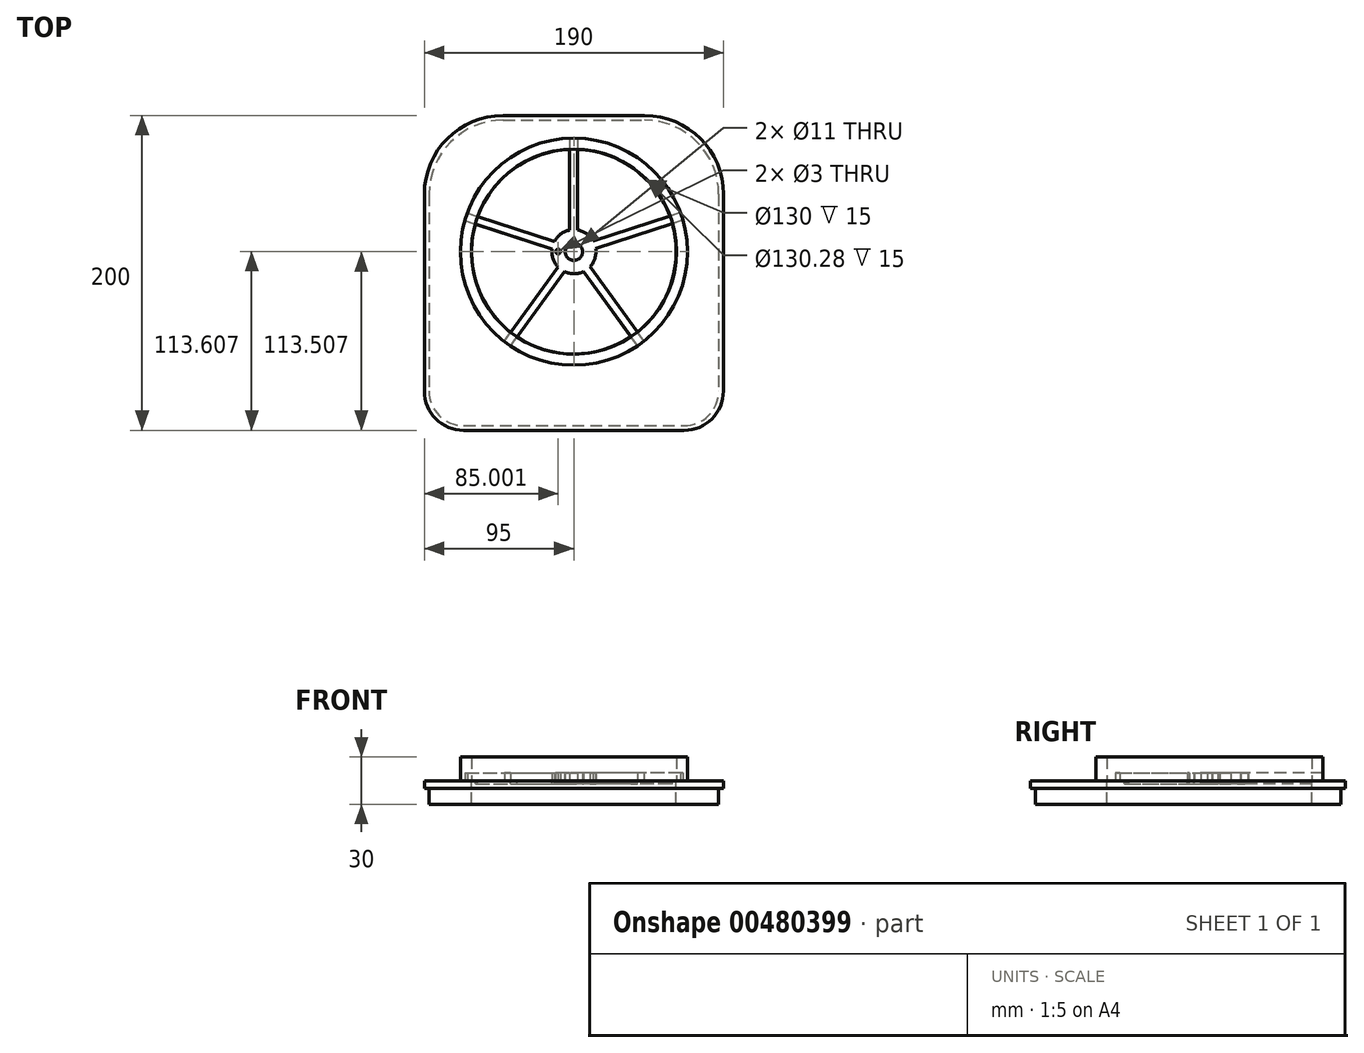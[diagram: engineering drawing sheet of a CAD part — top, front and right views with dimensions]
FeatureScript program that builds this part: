
annotation { "Feature Type Name" : "Feature", "Feature Type Description" : "" }
export const myFeature = defineFeature(function(context is Context, id is Id, definition is map)
    precondition{}
    {
        {
            var Q0;
            Q0=qCreatedBy(makeId("Top.planeOp"),FACE);
            var sketch = newSketch(context, id + "F0", { "sketchPlane" : qUnion([Q0])});
            skLineSegment(sketch, "E0.bottom", {"start": v(49, 200) * mm, "end": v(139, 200) * mm});
            skLineSegment(sketch, "E0.top", {"start": v(24, 0) * mm, "end": v(164, 0) * mm});
            skLineSegment(sketch, "E0.left", {"start": v(-1, 150) * mm, "end": v(-1, 25) * mm});
            skLineSegment(sketch, "E0.right", {"start": v(189, 150) * mm, "end": v(189, 25) * mm});
            skPoint(sketch, "E1.visualSharp", {"position": v(-1, 200) * mm});
            skArc(sketch, "E1.filletArc", {"start": v(49, 200) * mm, "mid": v(13.64, 185.36) * mm, "end": v(-1, 150) * mm});
            skPoint(sketch, "E2.visualSharp", {"position": v(189, 200) * mm});
            skArc(sketch, "E2.filletArc", {"start": v(189, 150) * mm, "mid": v(174.36, 185.36) * mm, "end": v(139, 200) * mm});
            skPoint(sketch, "E3.visualSharp", {"position": v(-1, 0) * mm});
            skArc(sketch, "E3.filletArc", {"start": v(-1, 25) * mm, "mid": v(6.32, 7.32) * mm, "end": v(24, 0) * mm});
            skPoint(sketch, "E4.visualSharp", {"position": v(189, 0) * mm});
            skArc(sketch, "E4.filletArc", {"start": v(164, 0) * mm, "mid": v(181.68, 7.32) * mm, "end": v(189, 25) * mm});
            skSolve(sketch);
        }
        {
            var Q0;
            Q0=makeQuery(id+"F0.imprint","IMPRINT",FACE,{"disambiguationData":[TD([[makeQuery(id+"F0.imprint","IMPRINT",EDGE,{"derivedFrom":sQuery(id+"F0.wireOp",EDGE,"E0.bottom")}),-1.0]])]});
            extrude(context, id + "F1", {"entities" : qUnion([Q0]), "depth" : 5 * mm});
        }
        {
            var Q0;
            Q0=makeQuery(id+"F1.opExtrude","CAP_FACE",FACE,{"disambiguationData":[OSD([sQuery(id+"F0.wireOp",EDGE,"E0.bottom"),sQuery(id+"F0.wireOp",EDGE,"E0.top"),sQuery(id+"F0.wireOp",EDGE,"E0.left"),sQuery(id+"F0.wireOp",EDGE,"E0.right"),sQuery(id+"F0.wireOp",EDGE,"E1.filletArc"),sQuery(id+"F0.wireOp",EDGE,"E2.filletArc"),sQuery(id+"F0.wireOp",EDGE,"E3.filletArc"),sQuery(id+"F0.wireOp",EDGE,"E4.filletArc")])],"isStart":true});
            var sketch = newSketch(context, id + "F2", { "sketchPlane" : qUnion([Q0])});
            skArc(sketch, "E5.0", {"start": v(186, -150) * mm, "mid": v(172.23, -183.23) * mm, "end": v(139, -197) * mm});
            skLineSegment(sketch, "E5.1", {"start": v(49, -197) * mm, "end": v(139, -197) * mm});
            skLineSegment(sketch, "E5.2", {"start": v(186, -150) * mm, "end": v(186, -25) * mm});
            skArc(sketch, "E5.3", {"start": v(49, -197) * mm, "mid": v(15.77, -183.23) * mm, "end": v(2, -150) * mm});
            skArc(sketch, "E5.4", {"start": v(164, -3) * mm, "mid": v(179.56, -9.44) * mm, "end": v(186, -25) * mm});
            skLineSegment(sketch, "E5.5", {"start": v(24, -3) * mm, "end": v(164, -3) * mm});
            skArc(sketch, "E5.6", {"start": v(2, -25) * mm, "mid": v(8.44, -9.44) * mm, "end": v(24, -3) * mm});
            skLineSegment(sketch, "E5.7", {"start": v(2, -150) * mm, "end": v(2, -25) * mm});
            skSolve(sketch);
        }
        {
            var Q0;
            Q0=makeQuery(id+"F2.imprint","IMPRINT",FACE,{"disambiguationData":[TD([[makeQuery(id+"F2.imprint","IMPRINT",EDGE,{"derivedFrom":sQuery(id+"F2.wireOp",EDGE,"E5.0")}),1.0]])]});
            extrude(context, id + "F3", {"entities" : qUnion([Q0]), "operationType" : NewBodyOperationType.ADD, "depth" : 10 * mm});
        }
        {
            var Q0;
            Q0=makeQuery(id+"F1.opExtrude","CAP_FACE",FACE,{"disambiguationData":[OSD([sQuery(id+"F0.wireOp",EDGE,"E0.bottom"),sQuery(id+"F0.wireOp",EDGE,"E0.top"),sQuery(id+"F0.wireOp",EDGE,"E0.left"),sQuery(id+"F0.wireOp",EDGE,"E0.right"),sQuery(id+"F0.wireOp",EDGE,"E1.filletArc"),sQuery(id+"F0.wireOp",EDGE,"E2.filletArc"),sQuery(id+"F0.wireOp",EDGE,"E3.filletArc"),sQuery(id+"F0.wireOp",EDGE,"E4.filletArc")])],"isStart":false});
            var sketch = newSketch(context, id + "F4", { "sketchPlane" : qUnion([Q0])});
            skCircle(sketch, "E6", {"center": v(94, 113.5) * mm, "radius": 65 * mm});
            skSolve(sketch);
        }
        {
            var Q0;
            Q0=makeQuery(id+"F4.imprint","IMPRINT",FACE,{"disambiguationData":[TD([[makeQuery(id+"F4.imprint","IMPRINT",EDGE,{"derivedFrom":sQuery(id+"F4.wireOp",EDGE,"E6")}),1.0]])]});
            extrude(context, id + "F5", {"entities" : qUnion([Q0]), "operationType" : NewBodyOperationType.REMOVE, "oppositeDirection" : true, "depth" : 25 * mm});
        }
        {
            var Q0;
            Q0=makeQuery(id+"F1.opExtrude","CAP_FACE",FACE,{"disambiguationData":[OSD([sQuery(id+"F0.wireOp",EDGE,"E0.bottom"),sQuery(id+"F0.wireOp",EDGE,"E0.top"),sQuery(id+"F0.wireOp",EDGE,"E0.left"),sQuery(id+"F0.wireOp",EDGE,"E0.right"),sQuery(id+"F0.wireOp",EDGE,"E1.filletArc"),sQuery(id+"F0.wireOp",EDGE,"E2.filletArc"),sQuery(id+"F0.wireOp",EDGE,"E3.filletArc"),sQuery(id+"F0.wireOp",EDGE,"E4.filletArc")])],"isStart":false});
            var sketch = newSketch(context, id + "F6", { "sketchPlane" : qUnion([Q0])});
            skArc(sketch, "E7", {"start": v(91.35, 127.25) * mm, "mid": v(85.65, 124.74) * mm, "end": v(81.6, 120) * mm});
            skLineSegment(sketch, "E8.left", {"start": v(91.35, 185.45) * mm, "end": v(91.35, 127.25) * mm});
            skLineSegment(sketch, "E8.right", {"start": v(96.35, 185.45) * mm, "end": v(96.35, 127.3) * mm});
            skLineSegment(sketch, "E9", {"start": v(91.35, 185.45) * mm, "end": v(96.35, 185.45) * mm});
            skLineSegment(sketch, "E10.1.0", {"start": v(24.76, 133.22) * mm, "end": v(80.1, 115.23) * mm});
            skLineSegment(sketch, "E10.1.1", {"start": v(26.3, 137.97) * mm, "end": v(81.6, 120) * mm});
            skLineSegment(sketch, "E10.1.3", {"start": v(24.76, 133.22) * mm, "end": v(26.3, 137.97) * mm});
            skLineSegment(sketch, "E10.2.0", {"start": v(53.86, 53.75) * mm, "end": v(88.06, 100.83) * mm});
            skLineSegment(sketch, "E10.2.1", {"start": v(49.81, 56.69) * mm, "end": v(83.99, 103.72) * mm});
            skLineSegment(sketch, "E10.2.3", {"start": v(53.86, 53.75) * mm, "end": v(49.81, 56.69) * mm});
            skLineSegment(sketch, "E10.3.0", {"start": v(138.43, 56.86) * mm, "end": v(104.22, 103.94) * mm});
            skLineSegment(sketch, "E10.3.1", {"start": v(134.39, 53.92) * mm, "end": v(100.21, 100.96) * mm});
            skLineSegment(sketch, "E10.3.3", {"start": v(138.43, 56.86) * mm, "end": v(134.39, 53.92) * mm});
            skLineSegment(sketch, "E10.4.0", {"start": v(161.6, 138.26) * mm, "end": v(106.25, 120.28) * mm});
            skLineSegment(sketch, "E10.4.1", {"start": v(163.15, 133.5) * mm, "end": v(107.85, 115.54) * mm});
            skLineSegment(sketch, "E10.4.3", {"start": v(161.6, 138.26) * mm, "end": v(163.15, 133.5) * mm});
            skArc(sketch, "E11.trimOffspring", {"start": v(106.25, 120.28) * mm, "mid": v(102.1, 124.92) * mm, "end": v(96.35, 127.3) * mm});
            skArc(sketch, "E12.trimOffspring", {"start": v(104.22, 103.94) * mm, "mid": v(107.36, 109.33) * mm, "end": v(107.85, 115.54) * mm});
            skArc(sketch, "E13.trimOffspring", {"start": v(88.06, 100.83) * mm, "mid": v(94.15, 99.5) * mm, "end": v(100.21, 100.96) * mm});
            skArc(sketch, "E14.trimOffspring", {"start": v(80.1, 115.23) * mm, "mid": v(80.73, 109.03) * mm, "end": v(83.99, 103.72) * mm});
            skCircle(sketch, "E15", {"center": v(94, 113.5) * mm, "radius": 5.5 * mm});
            skCircle(sketch, "E16", {"center": v(84, 113.6) * mm, "radius": 1.5 * mm});
            skSolve(sketch);
        }
        {
            var Q0;
            {var subQ13=sQuery(id+"F6.wireOp",EDGE,"E7");Q0=makeQuery(id+"F6.imprint","IMPRINT",FACE,{"disambiguationData":[TD([[makeQuery(id+"F6.imprint","IMPRINT",EDGE,{"derivedFrom":subQ13}),1.0]])]});}
            extrude(context, id + "F7", {"entities" : qUnion([Q0]), "oppositeDirection" : true, "depth" : 2 * mm});
        }
        {
            var Q0;
            Q0=makeQuery(id+"F7.opExtrude","CAP_FACE",FACE,{"disambiguationData":[OSD([sQuery(id+"F6.wireOp",EDGE,"E7"),sQuery(id+"F6.wireOp",EDGE,"E8.left"),sQuery(id+"F6.wireOp",EDGE,"E8.right"),sQuery(id+"F6.wireOp",EDGE,"E9"),sQuery(id+"F6.wireOp",EDGE,"E10.1.0"),sQuery(id+"F6.wireOp",EDGE,"E10.1.1"),sQuery(id+"F6.wireOp",EDGE,"E10.1.3"),sQuery(id+"F6.wireOp",EDGE,"E10.2.0"),sQuery(id+"F6.wireOp",EDGE,"E10.2.1"),sQuery(id+"F6.wireOp",EDGE,"E10.2.3"),sQuery(id+"F6.wireOp",EDGE,"E10.3.0"),sQuery(id+"F6.wireOp",EDGE,"E10.3.1"),sQuery(id+"F6.wireOp",EDGE,"E10.3.3"),sQuery(id+"F6.wireOp",EDGE,"E10.4.0"),sQuery(id+"F6.wireOp",EDGE,"E10.4.1"),sQuery(id+"F6.wireOp",EDGE,"E10.4.3"),sQuery(id+"F6.wireOp",EDGE,"E11.trimOffspring"),sQuery(id+"F6.wireOp",EDGE,"E12.trimOffspring"),sQuery(id+"F6.wireOp",EDGE,"E13.trimOffspring"),sQuery(id+"F6.wireOp",EDGE,"E14.trimOffspring")])],"isStart":false});
            var sketch = newSketch(context, id + "F8", { "sketchPlane" : qUnion([Q0])});
            skCircle(sketch, "E17", {"center": v(94, -113.5) * mm, "radius": 5 * mm});
            skSolve(sketch);
        }
        {
            var Q0;
            Q0=makeQuery(id+"F8.imprint","IMPRINT",FACE,{"disambiguationData":[TD([[makeQuery(id+"F8.imprint","IMPRINT",EDGE,{"derivedFrom":sQuery(id+"F8.wireOp",EDGE,"E17")}),1.0]])]});
            extrude(context, id + "F9", {"entities" : qUnion([Q0]), "operationType" : NewBodyOperationType.REMOVE, "oppositeDirection" : true, "depth" : 25 * mm});
        }
        {
            var Q0;
            Q0=makeQuery(id+"F7.opExtrude","CAP_FACE",FACE,{"disambiguationData":[OSD([sQuery(id+"F6.wireOp",EDGE,"E7"),sQuery(id+"F6.wireOp",EDGE,"E8.left"),sQuery(id+"F6.wireOp",EDGE,"E8.right"),sQuery(id+"F6.wireOp",EDGE,"E9"),sQuery(id+"F6.wireOp",EDGE,"E10.1.0"),sQuery(id+"F6.wireOp",EDGE,"E10.1.1"),sQuery(id+"F6.wireOp",EDGE,"E10.1.3"),sQuery(id+"F6.wireOp",EDGE,"E10.2.0"),sQuery(id+"F6.wireOp",EDGE,"E10.2.1"),sQuery(id+"F6.wireOp",EDGE,"E10.2.3"),sQuery(id+"F6.wireOp",EDGE,"E10.3.0"),sQuery(id+"F6.wireOp",EDGE,"E10.3.1"),sQuery(id+"F6.wireOp",EDGE,"E10.3.3"),sQuery(id+"F6.wireOp",EDGE,"E10.4.0"),sQuery(id+"F6.wireOp",EDGE,"E10.4.1"),sQuery(id+"F6.wireOp",EDGE,"E10.4.3"),sQuery(id+"F6.wireOp",EDGE,"E11.trimOffspring"),sQuery(id+"F6.wireOp",EDGE,"E12.trimOffspring"),sQuery(id+"F6.wireOp",EDGE,"E13.trimOffspring"),sQuery(id+"F6.wireOp",EDGE,"E14.trimOffspring")])],"isStart":false});
            var sketch = newSketch(context, id + "F10", { "sketchPlane" : qUnion([Q0])});
            skCircle(sketch, "E18", {"center": v(86, 113.5) * mm, "radius": 1.5 * mm});
            skCircle(sketch, "E19.1.0", {"center": v(94, 105.5) * mm, "radius": 1.5 * mm});
            skCircle(sketch, "E19.2.0", {"center": v(102, 113.5) * mm, "radius": 1.5 * mm});
            skCircle(sketch, "E19.3.0", {"center": v(94, 121.5) * mm, "radius": 1.5 * mm});
            skPoint(sketch, "E19.center", {"position": v(94, 113.5) * mm});
            skSolve(sketch);
        }
        {
            var Q0;
            Q0=makeQuery(id+"F10.imprint","IMPRINT",FACE,{"disambiguationData":[TD([[makeQuery(id+"F10.imprint","IMPRINT",EDGE,{"derivedFrom":sQuery(id+"F10.wireOp",EDGE,"E19.1.0")}),1.0]])]});
            var Q1;
            Q1=makeQuery(id+"F10.imprint","IMPRINT",FACE,{"disambiguationData":[TD([[makeQuery(id+"F10.imprint","IMPRINT",EDGE,{"derivedFrom":sQuery(id+"F10.wireOp",EDGE,"E18")}),1.0]])]});
            var Q2;
            Q2=makeQuery(id+"F10.imprint","IMPRINT",FACE,{"disambiguationData":[TD([[makeQuery(id+"F10.imprint","IMPRINT",EDGE,{"derivedFrom":sQuery(id+"F10.wireOp",EDGE,"E19.3.0")}),1.0]])]});
            var Q3;
            Q3=makeQuery(id+"F10.imprint","IMPRINT",FACE,{"disambiguationData":[TD([[makeQuery(id+"F10.imprint","IMPRINT",EDGE,{"derivedFrom":sQuery(id+"F10.wireOp",EDGE,"E19.2.0")}),1.0]])]});
            extrude(context, id + "F11", {"entities" : qUnion([Q0, Q1, Q2, Q3]), "operationType" : NewBodyOperationType.REMOVE, "oppositeDirection" : true, "depth" : 25 * mm});
        }
        {
            var Q0;
            Q0 = qSketchRegion(id + "F10", true);
            extrude(context, id + "F12", {"entities" : qUnion([Q0]), "operationType" : NewBodyOperationType.REMOVE, "oppositeDirection" : true, "depth" : 25 * mm});
        }
        {
            var Q0;
            Q0 = qSketchRegion(id + "F8", true);
            extrude(context, id + "F13", {"entities" : qUnion([Q0]), "operationType" : NewBodyOperationType.REMOVE, "oppositeDirection" : true, "depth" : 25 * mm});
        }
        {
            var Q0;
            Q0=makeQuery(id+"F1.opExtrude","CAP_FACE",FACE,{"disambiguationData":[OSD([sQuery(id+"F0.wireOp",EDGE,"E0.bottom"),sQuery(id+"F0.wireOp",EDGE,"E0.top"),sQuery(id+"F0.wireOp",EDGE,"E0.left"),sQuery(id+"F0.wireOp",EDGE,"E0.right"),sQuery(id+"F0.wireOp",EDGE,"E1.filletArc"),sQuery(id+"F0.wireOp",EDGE,"E2.filletArc"),sQuery(id+"F0.wireOp",EDGE,"E3.filletArc"),sQuery(id+"F0.wireOp",EDGE,"E4.filletArc")])],"isStart":false});
            var sketch = newSketch(context, id + "F14", { "sketchPlane" : qUnion([Q0])});
            skCircle(sketch, "E20", {"center": v(94, 113.5) * mm, "radius": 72.09 * mm});
            skCircle(sketch, "E21", {"center": v(94, 113.5) * mm, "radius": 65.14 * mm});
            skSolve(sketch);
        }
        {
            var Q0;
            Q0=makeQuery(id+"F14.imprint","IMPRINT",FACE,{"disambiguationData":[TD([[makeQuery(id+"F14.imprint","IMPRINT",EDGE,{"derivedFrom":sQuery(id+"F14.wireOp",EDGE,"E20")}),1.0]])]});
            extrude(context, id + "F15", {"entities" : qUnion([Q0]), "operationType" : NewBodyOperationType.ADD, "depth" : 15 * mm});
        }
        {
            var Q0;
            Q0 = qSketchRegion(id + "F6", true);
            extrude(context, id + "F16", {"entities" : qUnion([Q0]), "depth" : 5 * mm});
        }
    });
